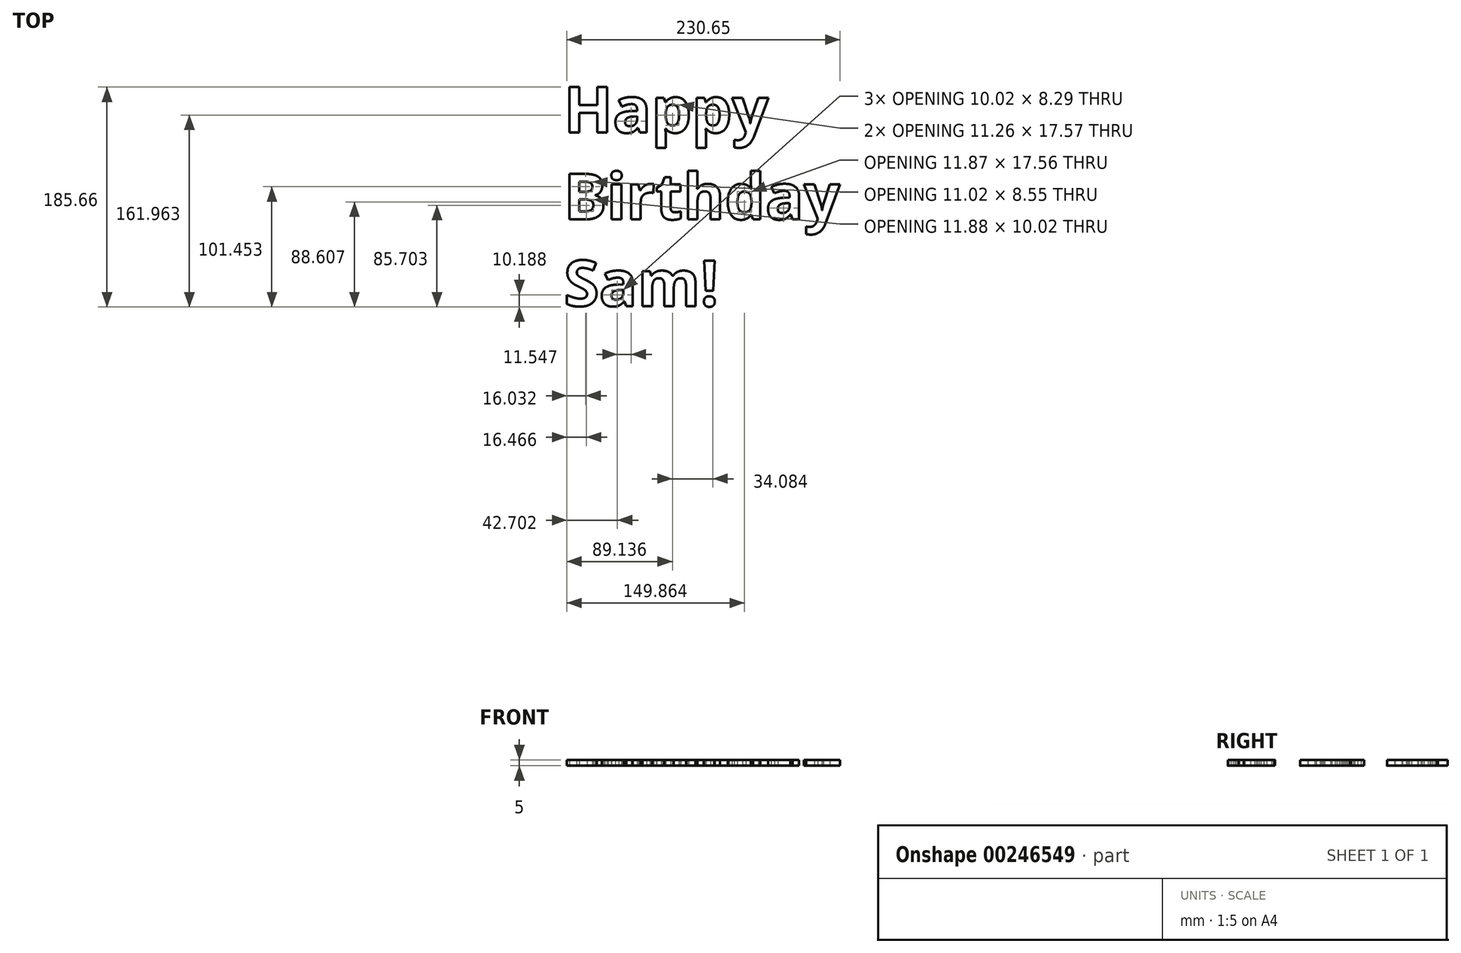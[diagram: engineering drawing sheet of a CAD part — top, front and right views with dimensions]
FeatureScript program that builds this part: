
annotation { "Feature Type Name" : "Feature", "Feature Type Description" : "" }
export const myFeature = defineFeature(function(context is Context, id is Id, definition is map)
    precondition{}
    {
        {
            var Q0;
            Q0=qCreatedBy(makeId("Top.planeOp"),FACE);
            var sketch = newSketch(context, id + "F0", { "sketchPlane" : qUnion([Q0])});
            skText(sketch, "E0", { "text": "Happy\nBirthday\nSam!", "fontName": "OpenSans-Bold.ttf"});
            const initialGuessF0  = {"E0": [0, 0, 1, 0, 0.03878]};
            skSetInitialGuess(sketch, initialGuessF0);
            skSolve(sketch);
        }
        {
            var Q0;
            Q0 = qSketchRegion(id + "F0", true);
            extrude(context, id + "F1", {"entities" : qUnion([Q0]), "depth" : 5 * mm});
        }
    });
